# Revit family: Fixture_Support_Water_Closet_Vertical-Zurn-Z1202-N4-FMBO-High-Performance
name_source: partatom
category: Plumbing Fixtures
units: mm (PartAtom-declared; Revit-internal decimal feet)

## family parameters
Always vertical = Yes
Cut with Voids When Loaded = No
Maintain Annotation Orientation = No
OmniClass Number = 23.45.55.11
OmniClass Title = Sanitary Components
Part Type = Normal
Room Calculation Point = No
Round Connector Dimension = Use Radius
Shared = No
Work Plane-Based = No

## types (1)
- Z1202-N4-FMBO
    Approx. Weight (Lbs) = 58.00 lb
    Assembly Code = D2030400
    CW Connection = No
    CWFU = 0
    Coupling Material = ABS - Zurn - Plastic
    Default Elevation = 20 "
    Description = EZCARRY® ADJUSTABLE VERTICAL HIGH PERFORMANCE SIPHON JET NO-HUB WATER CLOSET CARRIER SYSTEM  W/ FLOOR MOUNT BACK OUTLET FIXTURE SUPPORT
    HW Connection = No
    HWFU = 0
    J_ Verical Pipe Length = 24 "
    Main Material = Iron - Zurn - Cast - Painted - Blue
    Manufacturer = Zurn Water, LLC
    Manufacurer Brand = Zurn
    Model = Z1202-N4-FMBO
    Modified Date = 01/30/2026
    P_Coupling Length = 2 "
    Product Documentation Link = https://files.zurn.com
    Product Page URL = https://www.bimobject.com
    Product data url = https://www.bimobject.com
    Sanitary Inlet Radius = 2 "
    Sanitary Outlet Radius = 2 "
    Stud Matarial = Steel - Zurn  - Galvanized
    URL = www.zurn.com
    Vent Connection = Yes
    Vent Connection Radius = 1 "
    Vent Diameter (Actual) = 2.375 "
    Vent Diameter (Nominal) = 2 "
    Verical Pipe Axis Location = 6.813 "
    Vertical Pipe Diameter (Actual) = 4.5 "
    Vertical Pipe Diameter (Inner) = 4.028 "
    Vertical Pipe Diameter (Nominal) = 4 "
    WFU = 1
    Waste Connection = Yes
    Water Closet Inlet Radius = 1.5 "
    Width = 13.25 "

## geometry (parser evidence)
native form markers: Sweep x12
no freeform markers — native parametric forms only
